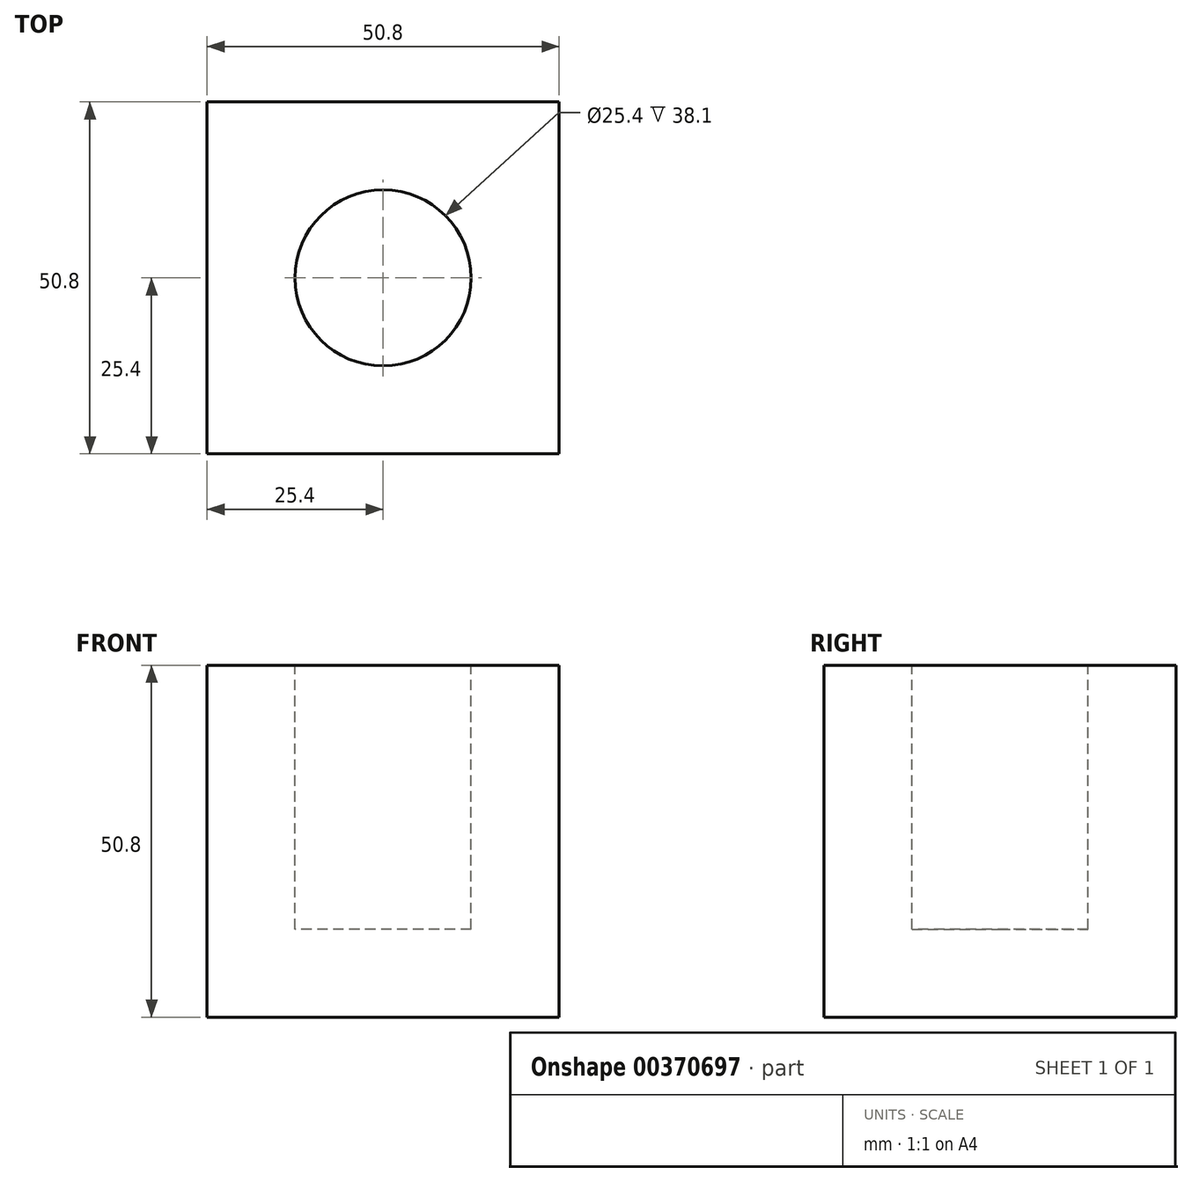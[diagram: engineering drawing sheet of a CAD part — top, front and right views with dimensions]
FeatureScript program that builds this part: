
annotation { "Feature Type Name" : "Feature", "Feature Type Description" : "" }
export const myFeature = defineFeature(function(context is Context, id is Id, definition is map)
    precondition{}
    {
        {
            var Q0;
            Q0=qCreatedBy(makeId("Top.planeOp"),FACE);
            var sketch = newSketch(context, id + "F0", { "sketchPlane" : qUnion([Q0])});
            skLineSegment(sketch, "E0", {"start": v(0, 0) * mm, "end": v(-50.8, 0) * mm});
            skLineSegment(sketch, "E1", {"start": v(-50.8, 0) * mm, "end": v(-50.8, 50.8) * mm});
            skLineSegment(sketch, "E2", {"start": v(-50.8, 50.8) * mm, "end": v(0, 50.8) * mm});
            skLineSegment(sketch, "E3", {"start": v(0, 50.8) * mm, "end": v(0, 0) * mm});
            skSolve(sketch);
        }
        {
            var Q0;
            Q0=makeQuery(id+"F0.imprint","IMPRINT",FACE,{"disambiguationData":[TD([[makeQuery(id+"F0.imprint","IMPRINT",EDGE,{"derivedFrom":sQuery(id+"F0.wireOp",EDGE,"E0")}),-1.0]])]});
            extrude(context, id + "F1", {"entities" : qUnion([Q0]), "depth" : 50.8 * mm});
        }
        {
            var Q0;
            Q0=makeQuery(id+"F1.opExtrude","CAP_FACE",FACE,{"disambiguationData":[OSD([sQuery(id+"F0.wireOp",EDGE,"E0"),sQuery(id+"F0.wireOp",EDGE,"E1"),sQuery(id+"F0.wireOp",EDGE,"E2"),sQuery(id+"F0.wireOp",EDGE,"E3")])],"isStart":false});
            var sketch = newSketch(context, id + "F2", { "sketchPlane" : qUnion([Q0])});
            skCircle(sketch, "E4", {"center": v(-25.4, 25.4) * mm, "radius": 12.7 * mm});
            skPoint(sketch, "E4.centerSnap0", {"position": v(-50.8, 25.4) * mm});
            skPoint(sketch, "E4.centerSnap1", {"position": v(-25.4, 0) * mm});
            skSolve(sketch);
        }
        {
            var Q0;
            Q0=makeQuery(id+"F2.imprint","IMPRINT",FACE,{"disambiguationData":[TD([[makeQuery(id+"F2.imprint","IMPRINT",EDGE,{"derivedFrom":sQuery(id+"F2.wireOp",EDGE,"E4")}),1.0]])]});
            extrude(context, id + "F3", {"entities" : qUnion([Q0]), "operationType" : NewBodyOperationType.REMOVE, "oppositeDirection" : true, "depth" : 38.1 * mm});
        }
    });
